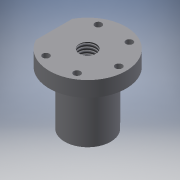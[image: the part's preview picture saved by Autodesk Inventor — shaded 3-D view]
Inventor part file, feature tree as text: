
AUTODESK INVENTOR PART (.ipt)
format: ipt  version: 2016 (Build 200138000, 138)  size: 182,784 bytes
history: native  units: mm
features: sketch x9, extrude x6, revolve x1, thread x1, plane x1
ambient origin geometry x8: Origin, YZ Plane, XZ Plane, XY Plane, X Axis, Y Axis, Z Axis, Center Point
bodies: Solid1 (feature_tree)
feature tree (18):
  revolve  "Revolution1"  [1 undecoded]
  extrude  "Extrusion1"  Depth=10.0mm
  extrude  "Extrusion2"  TaperAngle=90.0deg  [1 undecoded]
  thread  "Thread1"  [1 undecoded]
  extrude  "Extrusion3"  Depth=10.0mm TaperAngle=0.0deg
  plane  "Work Plane1"
  extrude  "Extrusion4"  Depth=10.0mm TaperAngle=0.0deg
  extrude  "Extrusion5"  Depth=10.0mm TaperAngle=0.0deg
  extrude  "Extrusion8"  Depth=8.0mm
  sketch  "Sketch21"  dims[d60=10.0mm d61=0.0mm]
  sketch  "Sketch22"  dims[d83=4.75mm d84=0.0mm d85=7.5mm d87=24.0mm d88=7.5mm]
  sketch  "Sketch1"  dims[d3=25.0mm d4=10.0mm]
  sketch  "Sketch2"  dims[d5=10.0mm d6=35.0mm]
  sketch  "Sketch3"  dims[d7=15.0mm d8=90.0deg d12=4.5mm]
  sketch  "Sketch4"  dims[d13=60.0mm d15=360.0deg d17=10.0mm d18=0.0mm]
  sketch  "Sketch5"  dims[d19=11.0mm d27=10.0mm d28=0.0mm]
  sketch  "Sketch9"  dims[d29=10.0mm d30=0.0mm d32=15.0mm d33=0.0mm]
  sketch  "Sketch20"  dims[d37=1.0mm d38=0.0mm d59=8.0mm]
note: 3 required parameter values undecoded (feature->parameter linkage not recoverable at this tier; creation-order binding heuristic only, values carry confidence <= 0.55)